# Revit family: 201_RAN-2-_
name_source: partatom
category: Air Terminals
units: mm (PartAtom-declared; Revit-internal decimal feet)

## family parameters
Always vertical = Yes
Cut with Voids When Loaded = No
Part Type = Normal
Room Calculation Point = Yes
Round Connector Dimension = Use Diameter
Shared = No
Work Plane-Based = No

## types (4) — shared parameters
CAT0 = Yes
CL_Location_5000 = 5000 mm  [stored 16.4042 ft]
CON1 = Yes
CON2 = No
CON3 = No
Description = Wall diffuser with plenum box, rear connection
F = 125 mm  [stored 0.410105 ft]
L_ARR = 400 mm  [stored 1.31234 ft]
Manufacturer = Climecon
QmdConnectorList = 201;D
URL = www.climecon.fi
W1 = 13 mm  [stored 0.0426509 ft]
W1__ve = -13 mm  [stored -0.0426509 ft]
W2 = 2 mm  [stored 0.00656168 ft]
W2__ve = -2 mm  [stored -0.00656168 ft]
W_ARR = 400 mm  [stored 1.31234 ft]
XRefLineVPlnId = 7453
YRefLineVPlnId = 7456
magiPartTypeId = 201
magiProductFamilyId = RAN-2-*
zero-valued in all types: CLBTZ, H_ARR, MC_Default_elevation

## per-type parameters (varying)
| type | A1 | B1 | D | H1 | H2 | L1 | W3 |
| RAN-2-100 | 225 mm  [stored 0.738189 ft] | 98 mm | 100 mm | 75 mm  [stored 0.246063 ft] | 65 mm  [stored 0.213255 ft] | 200 mm  [stored 0.656168 ft] | 160 mm  [stored 0.524934 ft] |
| RAN-2-200 | 325 mm  [stored 1.06627 ft] | 148 mm | 200 mm | 125 mm  [stored 0.410105 ft] | 97 mm  [stored 0.318241 ft] | 300 mm  [stored 0.984252 ft] | 225 mm  [stored 0.738189 ft] |
| RAN-2-160 | 275 mm  [stored 0.902231 ft] | 120 mm  [stored 0.393701 ft] | 160 mm | 100 mm  [stored 0.328084 ft] | 80 mm  [stored 0.262467 ft] | 250 mm  [stored 0.82021 ft] | 195 mm  [stored 0.639764 ft] |
| RAN-2-125 | 275 mm  [stored 0.902231 ft] | 98 mm | 125 mm | 75 mm  [stored 0.246063 ft] | 65 mm  [stored 0.213255 ft] | 250 mm  [stored 0.82021 ft] | 160 mm  [stored 0.524934 ft] |

note: column(s) folded — value = type name in every type: magiProductCode, magiProductId

note: [stored X ft] marks values corroborated as IEEE doubles in the binary element streams (Revit-internal decimal feet)

## geometry (parser evidence)
native form markers: Sweep x2
no freeform markers — native parametric forms only
